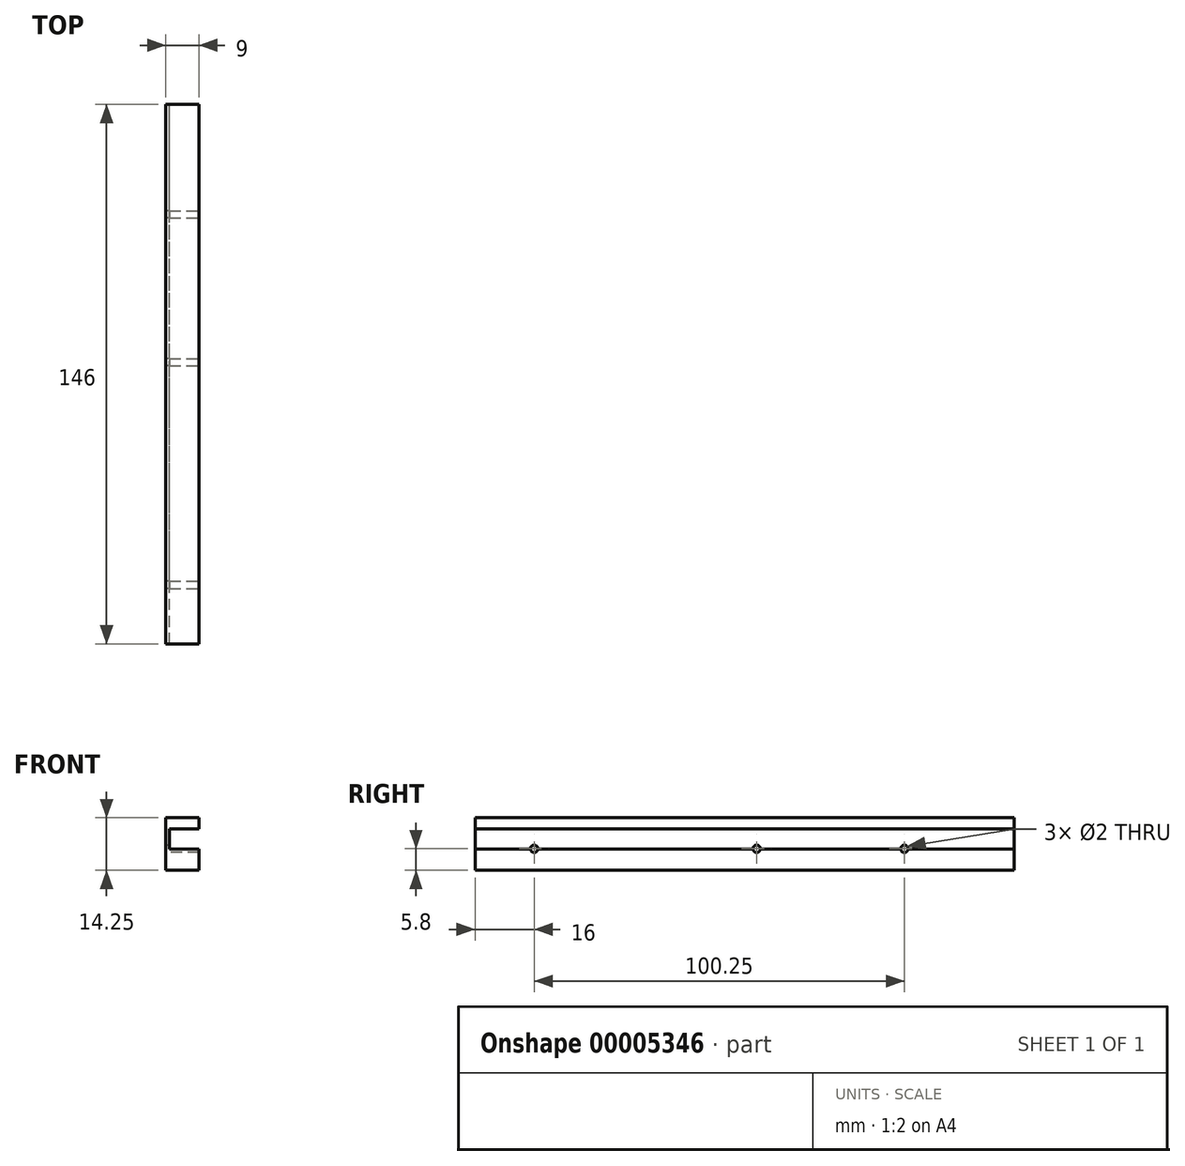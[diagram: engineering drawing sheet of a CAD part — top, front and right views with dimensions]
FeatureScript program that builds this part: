
annotation { "Feature Type Name" : "Feature", "Feature Type Description" : "" }
export const myFeature = defineFeature(function(context is Context, id is Id, definition is map)
    precondition{}
    {
        {
            var Q0;
            Q0=qCreatedBy(makeId("Right.planeOp"),FACE);
            var sketch = newSketch(context, id + "F0", { "sketchPlane" : qUnion([Q0])});
            skLineSegment(sketch, "E0.bottom", {"start": v(0, 0) * mm, "end": v(147, 0) * mm, "construction": true});
            skLineSegment(sketch, "E0.top", {"start": v(0, 15.25) * mm, "end": v(147, 15.25) * mm, "construction": true});
            skLineSegment(sketch, "E0.left", {"start": v(0, 0) * mm, "end": v(0, 15.25) * mm, "construction": true});
            skLineSegment(sketch, "E0.right", {"start": v(147, 0) * mm, "end": v(147, 15.25) * mm, "construction": true});
            skLineSegment(sketch, "E1", {"start": v(0, 10.75) * mm, "end": v(147, 10.75) * mm, "construction": true});
            skLineSegment(sketch, "E2", {"start": v(0, 7.25) * mm, "end": v(147, 7.25) * mm, "construction": true});
            skLineSegment(sketch, "E3", {"start": v(14.75, 7.25) * mm, "end": v(14.75, 10.75) * mm, "construction": true});
            skLineSegment(sketch, "E4", {"start": v(14.75, 10.75) * mm, "end": v(20.8, 10.75) * mm, "construction": true});
            skLineSegment(sketch, "E5", {"start": v(20.8, 10.75) * mm, "end": v(20.8, 8.08) * mm, "construction": true});
            skLineSegment(sketch, "E6", {"start": v(20.8, 8.08) * mm, "end": v(27.51, 8.08) * mm, "construction": true});
            skLineSegment(sketch, "E7", {"start": v(27.51, 8.08) * mm, "end": v(27.51, 7.25) * mm, "construction": true});
            skLineSegment(sketch, "E8", {"start": v(27.51, 7.25) * mm, "end": v(14.75, 7.25) * mm, "construction": true});
            skLineSegment(sketch, "E9.bottom", {"start": v(115, 10.75) * mm, "end": v(117.5, 10.75) * mm, "construction": true});
            skLineSegment(sketch, "E9.top", {"start": v(115, 7.25) * mm, "end": v(117.5, 7.25) * mm, "construction": true});
            skLineSegment(sketch, "E9.left", {"start": v(117.5, 10.75) * mm, "end": v(117.5, 7.25) * mm, "construction": true});
            skLineSegment(sketch, "E9.right", {"start": v(115, 10.75) * mm, "end": v(115, 7.25) * mm, "construction": true});
            skLineSegment(sketch, "E10", {"start": v(0, 6.3) * mm, "end": v(147, 6.3) * mm, "construction": true});
            skCircle(sketch, "E11", {"center": v(16.5, 6.3) * mm, "radius": 1 * mm});
            skCircle(sketch, "E12", {"center": v(76.75, 6.3) * mm, "radius": 1 * mm});
            skCircle(sketch, "E13", {"center": v(116.75, 6.3) * mm, "radius": 1 * mm});
            skLineSegment(sketch, "E14.0", {"start": v(0.5, 0.5) * mm, "end": v(146.5, 0.5) * mm});
            skLineSegment(sketch, "E14.1", {"start": v(0.5, 0.5) * mm, "end": v(0.5, 14.75) * mm});
            skLineSegment(sketch, "E14.2", {"start": v(0.5, 14.75) * mm, "end": v(146.5, 14.75) * mm});
            skLineSegment(sketch, "E14.3", {"start": v(146.5, 0.5) * mm, "end": v(146.5, 14.75) * mm});
            skSolve(sketch);
        }
        {
            var Q0;
            Q0 = qSketchRegion(id + "F0", true);
            extrude(context, id + "F1", {"entities" : qUnion([Q0]), "depth" : 9 * mm});
        }
        {
            var Q0;
            Q0=makeQuery(id+"F1.opExtrude","CAP_FACE",FACE,{"disambiguationData":[OSD([sQuery(id+"F0.wireOp",EDGE,"E11"),sQuery(id+"F0.wireOp",EDGE,"E12"),sQuery(id+"F0.wireOp",EDGE,"E13"),sQuery(id+"F0.wireOp",EDGE,"E14.0"),sQuery(id+"F0.wireOp",EDGE,"E14.1"),sQuery(id+"F0.wireOp",EDGE,"E14.2"),sQuery(id+"F0.wireOp",EDGE,"E14.3")])],"isStart":false});
            var sketch = newSketch(context, id + "F2", { "sketchPlane" : qUnion([Q0])});
            skPoint(sketch, "E15.0", {"position": v(0, 10.75) * mm});
            skPoint(sketch, "E16.0", {"position": v(147, 7.25) * mm});
            skLineSegment(sketch, "E17.bottom", {"start": v(0, 10.75) * mm, "end": v(147, 10.75) * mm, "construction": true});
            skLineSegment(sketch, "E17.top", {"start": v(0, 7.25) * mm, "end": v(147, 7.25) * mm, "construction": true});
            skLineSegment(sketch, "E17.left", {"start": v(0, 10.75) * mm, "end": v(0, 7.25) * mm, "construction": true});
            skLineSegment(sketch, "E17.right", {"start": v(147, 10.75) * mm, "end": v(147, 7.25) * mm, "construction": true});
            skLineSegment(sketch, "E18.0", {"start": v(-1, 11.75) * mm, "end": v(-1, 6.25) * mm});
            skLineSegment(sketch, "E18.1", {"start": v(-1, 11.75) * mm, "end": v(148, 11.75) * mm});
            skLineSegment(sketch, "E18.2", {"start": v(148, 11.75) * mm, "end": v(148, 6.25) * mm});
            skLineSegment(sketch, "E18.3", {"start": v(-1, 6.25) * mm, "end": v(148, 6.25) * mm});
            skSolve(sketch);
        }
        {
            var Q0;
            {var subQ12=sQuery(id+"F2.wireOp",EDGE,"E18.1");var subQ14=makeQuery(id+"F1.opExtrude","CAP_EDGE",EDGE,{"disambiguationData":[OSD([sQuery(id+"F0.wireOp",EDGE,"E14.1")])],"isStart":false});var subQ16=makeQuery(id+"F2.imprint","INTERSECT",VERTEX,{"derivedFrom":[subQ14,subQ12]});Q0=makeQuery(id+"F2.imprint","IMPRINT",FACE,{"disambiguationData":[TD([[makeQuery(id+"F2.imprint","IMPRINT",EDGE,{"disambiguationData":[TD([[subQ16,-1.0]])],"derivedFrom":subQ12}),-1.0]])]});}
            var Q1;
            Q1=sQuery(id+"F2.wireOp",EDGE,"E18.2");
            var Q2;
            Q2=sQuery(id+"F2.wireOp",EDGE,"E18.1");
            var Q3;
            Q3=sQuery(id+"F2.wireOp",EDGE,"E18.3");
            var Q4;
            Q4=sQuery(id+"F2.wireOp",EDGE,"E18.0");
            extrude(context, id + "F3", {"entities" : qUnion([Q0]), "operationType" : NewBodyOperationType.REMOVE, "surfaceEntities" : qUnion([Q1, Q2, Q3, Q4]), "oppositeDirection" : true, "depth" : 8 * mm});
        }
    });
